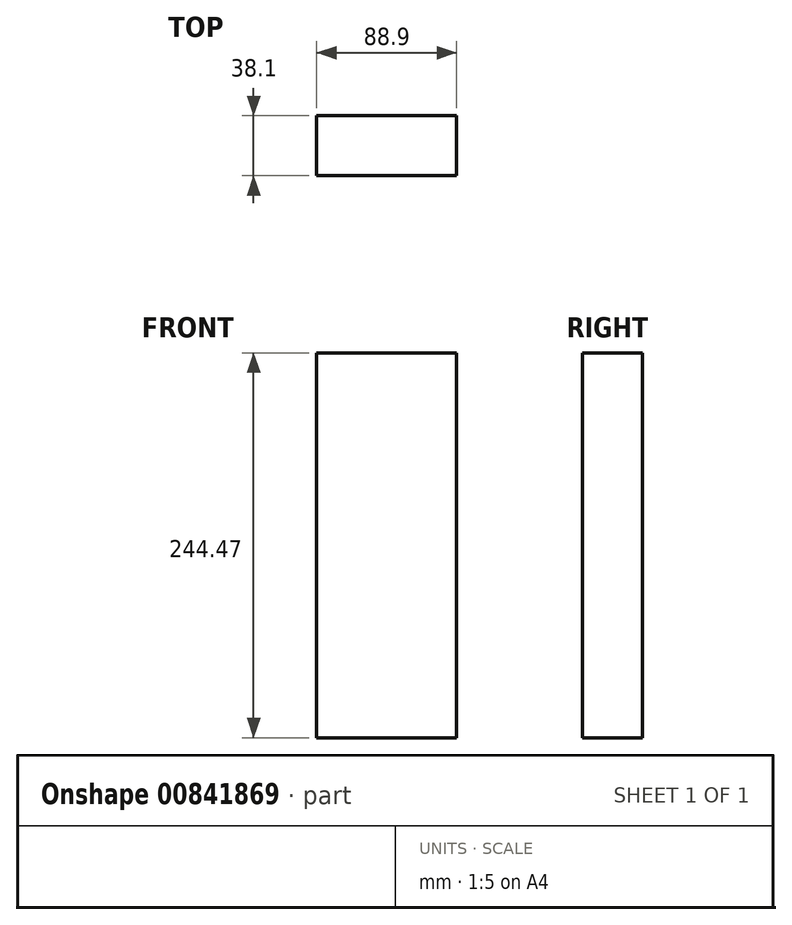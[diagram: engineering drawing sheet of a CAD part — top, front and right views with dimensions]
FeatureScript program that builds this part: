
annotation { "Feature Type Name" : "Feature", "Feature Type Description" : "" }
export const myFeature = defineFeature(function(context is Context, id is Id, definition is map)
    precondition{}
    {
        {
            var Q0;
            Q0=qCreatedBy(makeId("Top.planeOp"),FACE);
            var sketch = newSketch(context, id + "F0", { "sketchPlane" : qUnion([Q0])});
            skLineSegment(sketch, "E0.bottom", {"start": v(-44.45, 19.05) * mm, "end": v(44.45, 19.05) * mm});
            skLineSegment(sketch, "E0.top", {"start": v(-44.45, -19.05) * mm, "end": v(44.45, -19.05) * mm});
            skLineSegment(sketch, "E0.left", {"start": v(-44.45, 19.05) * mm, "end": v(-44.45, -19.05) * mm});
            skLineSegment(sketch, "E0.right", {"start": v(44.45, 19.05) * mm, "end": v(44.45, -19.05) * mm});
            skPoint(sketch, "E0.middle", {"position": v(0, 0) * mm});
            skSolve(sketch);
        }
        {
            var Q0;
            Q0 = qSketchRegion(id + "F0", true);
            extrude(context, id + "F1", {"entities" : qUnion([Q0]), "depth" : 244.47 * mm, "offsetDistance" : 25.4 * mm});
        }
    });
